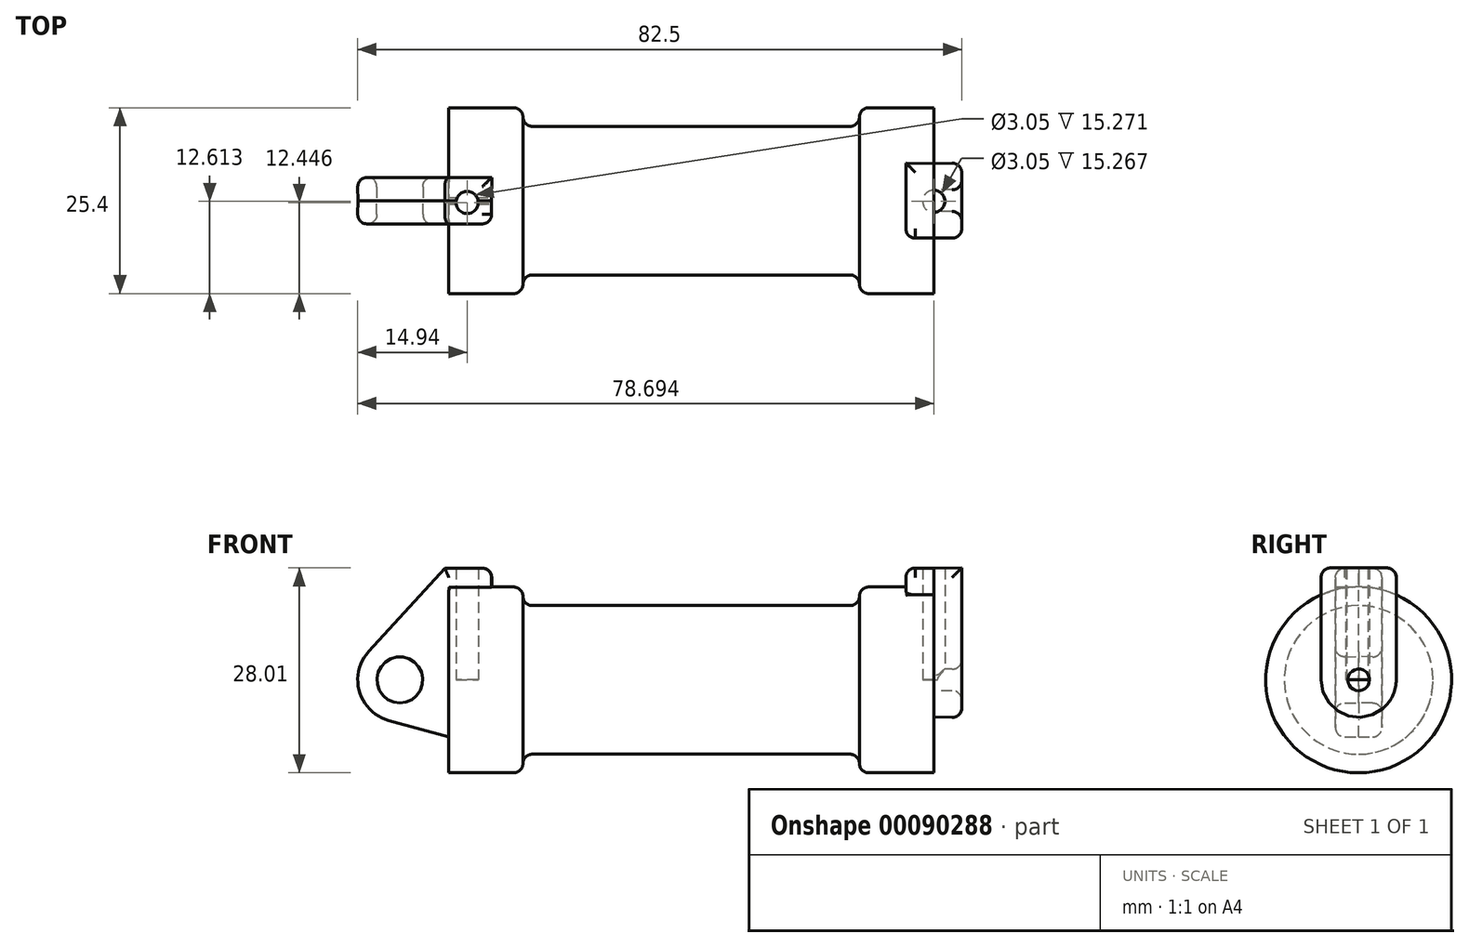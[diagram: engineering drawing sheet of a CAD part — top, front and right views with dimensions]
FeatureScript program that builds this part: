
annotation { "Feature Type Name" : "Feature", "Feature Type Description" : "" }
export const myFeature = defineFeature(function(context is Context, id is Id, definition is map)
    precondition{}
    {
        {
            var Q0;
            Q0=qCreatedBy(makeId("Front.planeOp"),FACE);
            var sketch = newSketch(context, id + "F0", { "sketchPlane" : qUnion([Q0])});
            skLineSegment(sketch, "E0", {"start": v(0, 0) * mm, "end": v(0, 12.7) * mm});
            skLineSegment(sketch, "E1", {"start": v(0, 12.7) * mm, "end": v(10.16, 12.7) * mm});
            skLineSegment(sketch, "E2", {"start": v(10.16, 12.7) * mm, "end": v(10.16, 10.16) * mm});
            skLineSegment(sketch, "E3", {"start": v(10.16, 10.16) * mm, "end": v(56.13, 10.16) * mm});
            skLineSegment(sketch, "E4", {"start": v(56.13, 10.16) * mm, "end": v(56.13, 12.7) * mm});
            skLineSegment(sketch, "E5", {"start": v(56.13, 12.7) * mm, "end": v(66.3, 12.7) * mm});
            skLineSegment(sketch, "E6", {"start": v(66.3, 12.7) * mm, "end": v(66.3, 0) * mm});
            skLineSegment(sketch, "E7", {"start": v(66.3, 0) * mm, "end": v(0, 0) * mm});
            skLineSegment(sketch, "E8", {"start": v(5.84, 15.24) * mm, "end": v(-0.5, 15.24) * mm});
            skLineSegment(sketch, "E9", {"start": v(-0.5, 15.24) * mm, "end": v(-10.88, 3.85) * mm});
            skLineSegment(sketch, "E10", {"start": v(0, 0) * mm, "end": v(-6.65, 0) * mm});
            skCircle(sketch, "E11", {"center": v(-6.65, 0) * mm, "radius": 5.72 * mm});
            skCircle(sketch, "E12", {"center": v(-6.65, 0) * mm, "radius": 3.18 * mm});
            skLineSegment(sketch, "E13", {"start": v(5.84, 15.24) * mm, "end": v(5.84, -9.4) * mm});
            skLineSegment(sketch, "E14", {"start": v(5.84, -9.4) * mm, "end": v(-8.18, -5.5) * mm});
            skSolve(sketch);
        }
        {
            var Q0;
            {var subQ0=sQuery(id+"F0.wireOp",EDGE,"E2");Q0=makeQuery(id+"F0.imprint","IMPRINT",FACE,{"disambiguationData":[TD([[makeQuery(id+"F0.imprint","IMPRINT",EDGE,{"derivedFrom":subQ0}),-1.0]])]});}
            var Q1;
            {var subQ0=sQuery(id+"F0.wireOp",EDGE,"E0");Q1=makeQuery(id+"F0.imprint","IMPRINT",FACE,{"disambiguationData":[TD([[makeQuery(id+"F0.imprint","IMPRINT",EDGE,{"derivedFrom":subQ0}),-1.0]])]});}
            var Q2;
            Q2=sQuery(id+"F0.wireOp",EDGE,"E7");
            revolve(context, id + "F1", {"entities" : qUnion([Q0, Q1]), "axis" : qUnion([Q2]), "revolveType" : RevolveType.FULL});
        }
        {
            var Q0;
            {var subQ3=sQuery(id+"F0.wireOp",EDGE,"E0");Q0=makeQuery(id+"F0.imprint","IMPRINT",FACE,{"disambiguationData":[TD([[makeQuery(id+"F0.imprint","IMPRINT",EDGE,{"derivedFrom":subQ3}),1.0]])]});}
            var Q1;
            {var subQ4=sQuery(id+"F0.wireOp",EDGE,"E12");Q1=makeQuery(id+"F0.imprint","IMPRINT",FACE,{"disambiguationData":[TD([[makeQuery(id+"F0.imprint","IMPRINT",EDGE,{"derivedFrom":subQ4}),-1.0]])]});}
            var Q2;
            {var subQ0=sQuery(id+"F0.wireOp",EDGE,"E14");Q2=makeQuery(id+"F0.imprint","IMPRINT",FACE,{"disambiguationData":[TD([[makeQuery(id+"F0.imprint","IMPRINT",EDGE,{"derivedFrom":subQ0}),-1.0]])]});}
            extrude(context, id + "F2", {"entities" : qUnion([Q0, Q1, Q2]), "operationType" : NewBodyOperationType.ADD, "endBound" : BoundingType.SYMMETRIC, "depth" : 6.35 * mm, "hasDraft" : true, "draftAngle" : 1 * degree});
        }
        {
            var Q0;
            Q0=makeQuery(id+"F1.opRevolve","SWEPT_FACE",FACE,{"disambiguationData":[OSD([sQuery(id+"F0.wireOp",EDGE,"E6")])]});
            var sketch = newSketch(context, id + "F3", { "sketchPlane" : qUnion([Q0])});
            skCircle(sketch, "E15", {"center": v(0, 0) * mm, "radius": 1.52 * mm});
            skCircle(sketch, "E16", {"center": v(0, 0) * mm, "radius": 5.08 * mm});
            skLineSegment(sketch, "E17", {"start": v(5.08, 0) * mm, "end": v(5.08, 15.24) * mm});
            skLineSegment(sketch, "E18", {"start": v(-5.08, 0) * mm, "end": v(-5.08, 15.24) * mm});
            skLineSegment(sketch, "E19", {"start": v(-5.08, 15.24) * mm, "end": v(5.08, 15.24) * mm});
            skSolve(sketch);
        }
        {
            var Q0;
            Q0 = qSketchRegion(id + "F3", true);
            extrude(context, id + "F4", {"entities" : qUnion([Q0]), "operationType" : NewBodyOperationType.ADD, "endBound" : BoundingType.SYMMETRIC, "depth" : 7.62 * mm, "hasDraft" : true, "draftAngle" : 1 * degree});
        }
        {
            var Q0;
            Q0=qCreatedBy(makeId("Top.planeOp"),FACE);
            var sketch = newSketch(context, id + "F5", { "sketchPlane" : qUnion([Q0])});
            skCircle(sketch, "E20", {"center": v(2.54, -0.25) * mm, "radius": 1.52 * mm});
            skSolve(sketch);
        }
        {
            var Q0;
            Q0 = qSketchRegion(id + "F5", true);
            extrude(context, id + "F6", {"entities" : qUnion([Q0]), "operationType" : NewBodyOperationType.REMOVE, "depth" : 17.78 * mm});
        }
        {
            var Q0;
            Q0=qCreatedBy(makeId("Top.planeOp"),FACE);
            var sketch = newSketch(context, id + "F7", { "sketchPlane" : qUnion([Q0])});
            skCircle(sketch, "E21", {"center": v(66.3, -0.09) * mm, "radius": 1.52 * mm});
            skSolve(sketch);
        }
        {
            var Q0;
            Q0 = qSketchRegion(id + "F7", true);
            extrude(context, id + "F8", {"entities" : qUnion([Q0]), "operationType" : NewBodyOperationType.REMOVE, "endBound" : BoundingType.THROUGH_ALL, "depth" : 10.4 * mm});
        }
        {
            var Q0;
            Q0=makeQuery(id+"F1.opRevolve","SWEPT_FACE",FACE,{"disambiguationData":[OSD([sQuery(id+"F0.wireOp",EDGE,"E3")])]});
            var Q1;
            Q1=makeQuery(id+"F1.opRevolve","SWEPT_EDGE",EDGE,{"disambiguationData":[OSD([sQuery(id+"F0.wireOp",EDGE,"E4"),sQuery(id+"F0.wireOp",EDGE,"E5")])]});
            var Q2;
            Q2=makeQuery(id+"F4.opExtrude","CAP_EDGE",EDGE,{"disambiguationData":[OSD([sQuery(id+"F3.wireOp",EDGE,"E18")])],"isStart":false});
            var Q3;
            Q3=makeQuery(id+"F4.opExtrude","CAP_EDGE",EDGE,{"disambiguationData":[OSD([sQuery(id+"F3.wireOp",EDGE,"E18")])],"isStart":true});
            var Q4;
            {var subQ0=sQuery(id+"F0.wireOp",EDGE,"E13");Q4=makeQuery(id+"F2.opExtrude","CAP_EDGE",EDGE,{"disambiguationData":[OSD([subQ0]),TDD([makeQuery(id+"F0.imprint","IMPRINT",EDGE,{"disambiguationData":[TD([[makeQuery(id+"F0.imprint","INTERSECT",VERTEX,{"derivedFrom":[sQuery(id+"F0.wireOp",EDGE,"E8"),subQ0]}),-1.0]])],"derivedFrom":subQ0})])],"isStart":false});}
            var Q5;
            Q5=makeQuery(id+"F1.opRevolve","SWEPT_EDGE",EDGE,{"disambiguationData":[OSD([sQuery(id+"F0.wireOp",EDGE,"E1"),sQuery(id+"F0.wireOp",EDGE,"E2")])]});
            var Q6;
            Q6=makeQuery(id+"F2.opExtrude","CAP_EDGE",EDGE,{"disambiguationData":[OSD([sQuery(id+"F0.wireOp",EDGE,"E8")])],"isStart":false});
            var Q7;
            Q7=makeQuery(id+"F4.split0.splitOp","SPLIT",EDGE,{"derivedFrom":makeQuery(id+"F4.opExtrude","SWEPT_EDGE",EDGE,{"disambiguationData":[OSD([sQuery(id+"F3.wireOp",EDGE,"E18"),sQuery(id+"F3.wireOp",EDGE,"E19")])]}),"isFromBackBody":true});
            var Q8;
            Q8=makeQuery(id+"F4.split0.splitOp","SPLIT",EDGE,{"derivedFrom":makeQuery(id+"F4.opExtrude","SWEPT_EDGE",EDGE,{"disambiguationData":[OSD([sQuery(id+"F3.wireOp",EDGE,"E18"),sQuery(id+"F3.wireOp",EDGE,"E19")])]})});
            var Q9;
            Q9=makeQuery(id+"F2.opExtrude","CAP_EDGE",EDGE,{"disambiguationData":[OSD([sQuery(id+"F0.wireOp",EDGE,"E9")])],"isStart":false});
            var Q10;
            Q10=makeQuery(id+"F2.opExtrude","CAP_EDGE",EDGE,{"disambiguationData":[OSD([sQuery(id+"F0.wireOp",EDGE,"E14")])],"isStart":false});
            var Q11;
            Q11=makeQuery(id+"F2.split0.splitOp","SPLIT",EDGE,{"derivedFrom":makeQuery(id+"F2.opExtrude","SWEPT_EDGE",EDGE,{"disambiguationData":[OSD([sQuery(id+"F0.wireOp",EDGE,"E8"),sQuery(id+"F0.wireOp",EDGE,"E13")])]}),"isFromBackBody":true});
            var Q12;
            Q12=makeQuery(id+"F2.split0.splitOp","SPLIT",EDGE,{"derivedFrom":makeQuery(id+"F2.opExtrude","SWEPT_EDGE",EDGE,{"disambiguationData":[OSD([sQuery(id+"F0.wireOp",EDGE,"E8"),sQuery(id+"F0.wireOp",EDGE,"E13")])]})});
            var Q13;
            Q13=makeQuery(id+"F4.opExtrude","CAP_EDGE",EDGE,{"disambiguationData":[OSD([sQuery(id+"F3.wireOp",EDGE,"E19")])],"isStart":true});
            var Q14;
            Q14=makeQuery(id+"F4.split0.splitOp","SPLIT",EDGE,{"derivedFrom":makeQuery(id+"F4.opExtrude","SWEPT_EDGE",EDGE,{"disambiguationData":[OSD([sQuery(id+"F3.wireOp",EDGE,"E17"),sQuery(id+"F3.wireOp",EDGE,"E19")])]}),"isFromBackBody":true});
            var Q15;
            Q15=makeQuery(id+"F4.split0.splitOp","SPLIT",EDGE,{"derivedFrom":makeQuery(id+"F4.opExtrude","SWEPT_EDGE",EDGE,{"disambiguationData":[OSD([sQuery(id+"F3.wireOp",EDGE,"E17"),sQuery(id+"F3.wireOp",EDGE,"E19")])]})});
            var Q16;
            Q16=makeQuery(id+"F2.opExtrude","CAP_EDGE",EDGE,{"disambiguationData":[OSD([sQuery(id+"F0.wireOp",EDGE,"E8")])],"isStart":true});
            var Q17;
            Q17=makeQuery(id+"F2.opExtrude","CAP_EDGE",EDGE,{"disambiguationData":[OSD([sQuery(id+"F0.wireOp",EDGE,"E9")])],"isStart":true});
            var Q18;
            Q18=makeQuery(id+"F2.opExtrude","CAP_EDGE",EDGE,{"disambiguationData":[OSD([sQuery(id+"F0.wireOp",EDGE,"E12")])],"isStart":false});
            var Q19;
            Q19=makeQuery(id+"F2.opExtrude","CAP_EDGE",EDGE,{"disambiguationData":[OSD([sQuery(id+"F0.wireOp",EDGE,"E12")])],"isStart":true});
            var Q20;
            Q20=makeQuery(id+"F4.opExtrude","CAP_EDGE",EDGE,{"disambiguationData":[OSD([sQuery(id+"F3.wireOp",EDGE,"E15")])],"isStart":false});
            fillet(context, id + "F9", {"entities" : qUnion([Q0, Q1, Q2, Q3, Q4, Q5, Q6, Q7, Q8, Q9, Q10, Q11, Q12, Q13, Q14, Q15, Q16, Q17, Q18, Q19, Q20]), "radius" : 1.27 * mm, "tangentPropagation" : true, "allowEdgeOverflow" : false});
        }
    });
